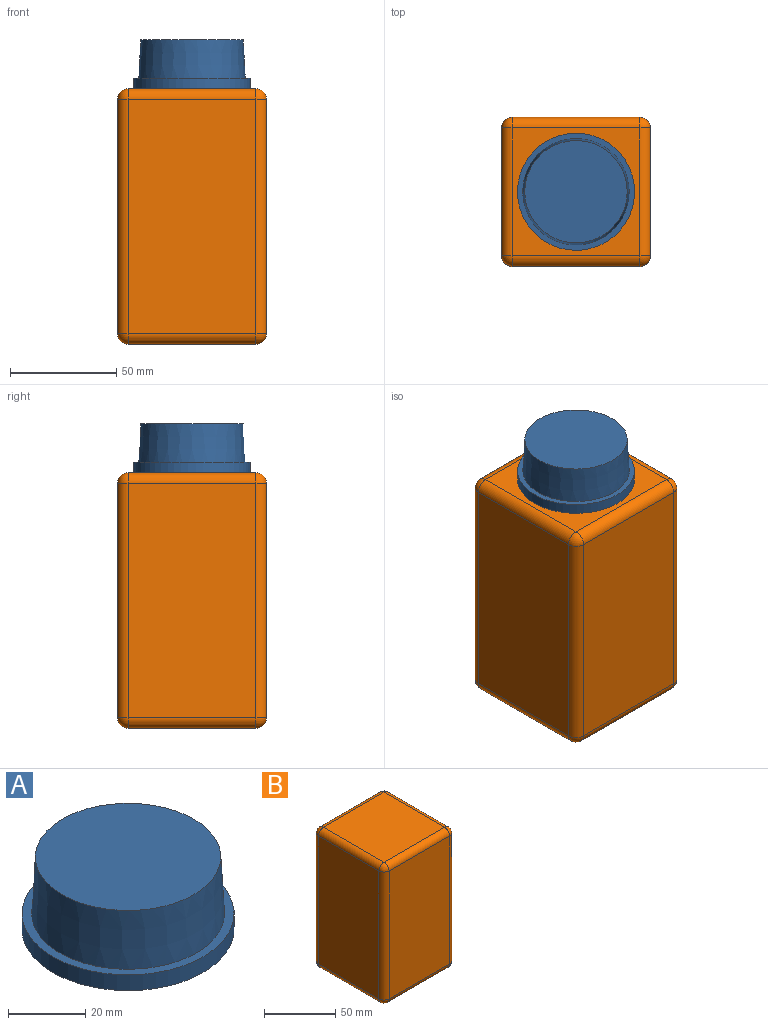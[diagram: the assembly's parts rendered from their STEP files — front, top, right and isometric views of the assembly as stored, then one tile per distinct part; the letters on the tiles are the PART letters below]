
ASSEMBLY  parts=2 mates=1
PART A: 5 faces, bbox 55x55x23 mm
  f0: cylinder r=27.5mm len=55mm, axis (0,0,-1), area 863.9mm2, adj f1,f2
  f1: plane 55x55mm, normal (0,0,1), area 412.3mm2, adj f0,f3
  f2: plane 55x55mm, normal (0,0,-1), area 2375.8mm2, adj f0
  f3: cone r=25mm half-angle=3deg, axis (0,0,-1), area 2777.9mm2, adj f1,f4
  f4: plane 48.11x48.11mm, normal (0,0,1), area 1818.1mm2, adj f3
PART B: 26 faces, bbox 70x70x120 mm
  f0: cylinder r=5mm len=110mm, axis (0,0,-1), area 863.9mm2, adj f1,f7,f14,f22
  f1: plane 110x60mm, normal (0,1,0), area 6600mm2, adj f0,f2,f12,f20
  f2: cylinder r=5mm len=110mm, axis (0,0,-1), area 863.9mm2, adj f1,f3,f10,f18
  f3: plane 110x60mm, normal (-1,0,0), area 6600mm2, adj f2,f4,f11,f19
  f4: cylinder r=5mm len=110mm, axis (0,0,-1), area 863.9mm2, adj f3,f5,f13,f21
  f5: plane 110x60mm, normal (0,-1,0), area 6600mm2, adj f4,f6,f15,f23
  f6: cylinder r=5mm len=110mm, axis (0,0,-1), area 863.9mm2, adj f5,f7,f17,f25
  f7: plane 110x60mm, normal (1,0,0), area 6600mm2, adj f0,f6,f16,f24
  f8: plane 60x60mm, normal (0,0,1), area 3600mm2, adj f19,f20,f23,f24
  f9: plane 60x60mm, normal (0,0,-1), area 3600mm2, adj f11,f12,f15,f16
  f10: sphere r=5mm, area 39.3mm2, adj f2,f11,f12
  f11: cylinder r=5mm len=60mm, axis (0,-1,0), area 471.2mm2, adj f3,f9,f10,f13
  f12: cylinder r=5mm len=60mm, axis (-1,0,0), area 471.2mm2, adj f1,f9,f10,f14
  f13: sphere r=5mm, area 39.3mm2, adj f4,f11,f15
  f14: sphere r=5mm, area 39.3mm2, adj f0,f12,f16
  f15: cylinder r=5mm len=60mm, axis (1,0,0), area 471.2mm2, adj f5,f9,f13,f17
  f16: cylinder r=5mm len=60mm, axis (0,1,0), area 471.2mm2, adj f7,f9,f14,f17
  f17: sphere r=5mm, area 39.3mm2, adj f6,f15,f16
  f18: sphere r=5mm, area 39.3mm2, adj f2,f19,f20
  f19: cylinder r=5mm len=60mm, axis (0,1,0), area 471.2mm2, adj f3,f8,f18,f21
  f20: cylinder r=5mm len=60mm, axis (1,0,0), area 471.2mm2, adj f1,f8,f18,f22
  f21: sphere r=5mm, area 39.3mm2, adj f4,f19,f23
  f22: sphere r=5mm, area 39.3mm2, adj f0,f20,f24
  f23: cylinder r=5mm len=60mm, axis (-1,0,0), area 471.2mm2, adj f5,f8,f21,f25
  f24: cylinder r=5mm len=60mm, axis (0,-1,0), area 471.2mm2, adj f7,f8,f22,f25
  f25: sphere r=5mm, area 39.3mm2, adj f6,f23,f24
PLACE A t=(0,0,120)mm
PLACE B t=(0,-0.18,0)mm
MATE cylindrical A.f0 <-> B.f8  axis (0,0,-1) through (0,0,120)mm
